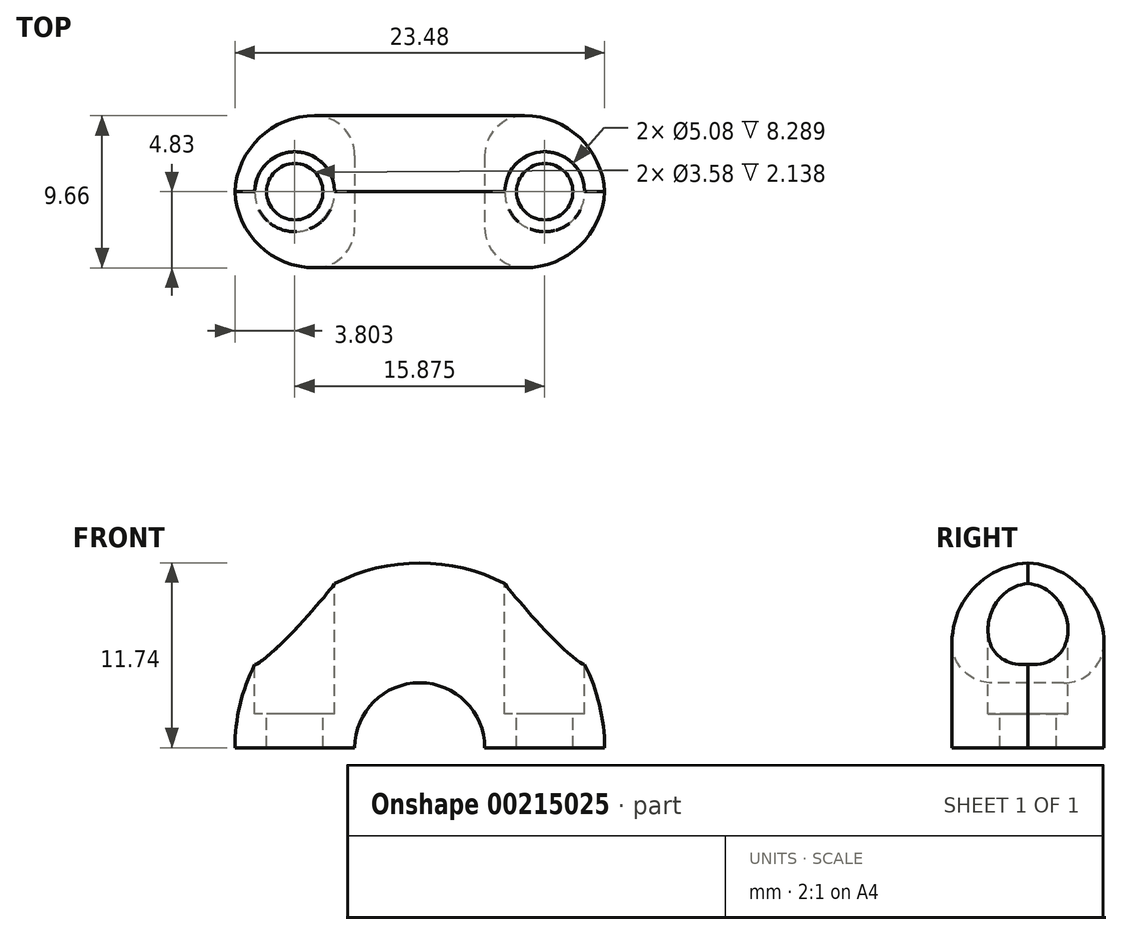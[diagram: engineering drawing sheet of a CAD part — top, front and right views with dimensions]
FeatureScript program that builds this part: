
annotation { "Feature Type Name" : "Feature", "Feature Type Description" : "" }
export const myFeature = defineFeature(function(context is Context, id is Id, definition is map)
    precondition{}
    {
        {
            var Q0;
            Q0=qCreatedBy(makeId("Top.planeOp"),FACE);
            var sketch = newSketch(context, id + "F0", { "sketchPlane" : qUnion([Q0])});
            skCircle(sketch, "E0", {"center": v(0, 0) * mm, "radius": 7.94 * mm, "construction": true});
            skCircle(sketch, "E1", {"center": v(-7.94, 0) * mm, "radius": 1.8 * mm});
            skLineSegment(sketch, "E2.bottom", {"start": v(14.29, 4.83) * mm, "end": v(-14.29, 4.83) * mm});
            skLineSegment(sketch, "E2.top", {"start": v(14.29, -4.83) * mm, "end": v(-14.29, -4.83) * mm});
            skLineSegment(sketch, "E2.left", {"start": v(14.29, 4.83) * mm, "end": v(14.29, -4.83) * mm});
            skLineSegment(sketch, "E2.right", {"start": v(-14.29, 4.83) * mm, "end": v(-14.29, -4.83) * mm});
            skCircle(sketch, "E3", {"center": v(-7.94, 0) * mm, "radius": 3.81 * mm});
            skLineSegment(sketch, "E4", {"start": v(0, 0) * mm, "end": v(0, 13.84) * mm, "construction": true});
            skCircle(sketch, "E5.MirrorC", {"center": v(7.94, 0) * mm, "radius": 1.8 * mm});
            skCircle(sketch, "E6.MirrorC", {"center": v(7.94, 0) * mm, "radius": 3.81 * mm});
            skLineSegment(sketch, "E7.bottom", {"start": v(-11.75, 4.83) * mm, "end": v(-4.13, 4.83) * mm});
            skLineSegment(sketch, "E7.top", {"start": v(-11.75, -4.83) * mm, "end": v(-4.13, -4.83) * mm});
            skLineSegment(sketch, "E7.left", {"start": v(-11.75, 4.83) * mm, "end": v(-11.75, -4.83) * mm});
            skLineSegment(sketch, "E7.right", {"start": v(-4.13, 4.83) * mm, "end": v(-4.13, -4.83) * mm});
            skSolve(sketch);
        }
        {
            var Q0;
            Q0=makeQuery(id+"F0.imprint","IMPRINT",FACE,{"disambiguationData":[TD([[makeQuery(id+"F0.imprint","IMPRINT",EDGE,{"derivedFrom":sQuery(id+"F0.wireOp",EDGE,"E1")}),-1.0]])]});
            var Q1;
            Q1=makeQuery(id+"F0.imprint","IMPRINT",FACE,{"disambiguationData":[TD([[makeQuery(id+"F0.imprint","IMPRINT",EDGE,{"derivedFrom":sQuery(id+"F0.wireOp",EDGE,"E1")}),1.0]])]});
            var Q2;
            Q2=makeQuery(id+"F0.imprint","IMPRINT",FACE,{"disambiguationData":[TD([[makeQuery(id+"F0.imprint","IMPRINT",EDGE,{"derivedFrom":sQuery(id+"F0.wireOp",EDGE,"E3")}),-1.0]])]});
            var Q3;
            Q3=sQuery(id+"F0.wireOp",EDGE,"E4");
            revolve(context, id + "F1", {"entities" : qUnion([Q0, Q1, Q2]), "axis" : qUnion([Q3]), "revolveType" : RevolveType.ONE_DIRECTION, "angle" : 180 * degree});
        }
        {
            var Q0;
            Q0=qCreatedBy(makeId("Top.planeOp"),FACE);
            cPlane(context, id + "F2", {"entities" : qUnion([Q0]), "cplaneType" : CPlaneType.OFFSET, "offset" : 12.7 * mm, "width" : 152.4 * mm, "height" : 152.4 * mm});
        }
        {
            var Q0;
            Q0=qCreatedBy(id+"F2.planeOp",FACE);
            var sketch = newSketch(context, id + "F3", { "sketchPlane" : qUnion([Q0])});
            skCircle(sketch, "E8", {"center": v(0, 0) * mm, "radius": 4.45 * mm});
            skCircle(sketch, "E9", {"center": v(0, 0) * mm, "radius": 7.94 * mm, "construction": true});
            skPoint(sketch, "E10", {"position": v(-7.94, 0) * mm});
            skPoint(sketch, "E11", {"position": v(7.94, 0) * mm});
            skSolve(sketch);
        }
        {
            var Q0;
            Q0=sQuery(id+"F3.wireOp",VERTEX,"E10");
            var Q1;
            Q1=sQuery(id+"F3.wireOp",VERTEX,"E11");
            var Q2;
            Q2=makeQuery(id+"F1.opRevolve","SWEPT_BODY",BODY,{"disambiguationData":[OSD([sQuery(id+"F0.wireOp",EDGE,"E7.bottom"),sQuery(id+"F0.wireOp",EDGE,"E7.top"),sQuery(id+"F0.wireOp",EDGE,"E7.left"),sQuery(id+"F0.wireOp",EDGE,"E7.right")])]});
            hole(context, id + "F4", {"style" : HoleStyle.C_BORE, "endStyle" : HoleEndStyle.BLIND, "holeDiameter" : 3.58 * mm, "cBoreDiameter" : 5.08 * mm, "cBoreDepth" : 3.17 * mm, "holeDepth" : 9.65 * mm, "locations" : qUnion([Q0, Q1]), "scope" : qUnion([Q2])});
        }
        {
            var Q0;
            Q0=makeQuery(id+"F1.opRevolve","SWEPT_EDGE",EDGE,{"disambiguationData":[OSD([sQuery(id+"F0.wireOp",EDGE,"E2.top"),sQuery(id+"F0.wireOp",EDGE,"E7.top"),sQuery(id+"F0.wireOp",EDGE,"E7.left")])]});
            var Q1;
            Q1=makeQuery(id+"F1.opRevolve","SWEPT_EDGE",EDGE,{"disambiguationData":[OSD([sQuery(id+"F0.wireOp",EDGE,"E2.bottom"),sQuery(id+"F0.wireOp",EDGE,"E7.bottom"),sQuery(id+"F0.wireOp",EDGE,"E7.left")])]});
            fillet(context, id + "F5", {"entities" : qUnion([Q0, Q1]), "radius" : 5.08 * mm, "tangentPropagation" : true, "allowEdgeOverflow" : false});
        }
        {
            var Q0;
            Q0=makeQuery(id+"F1.opRevolve","SWEPT_EDGE",EDGE,{"disambiguationData":[OSD([sQuery(id+"F0.wireOp",EDGE,"E2.top"),sQuery(id+"F0.wireOp",EDGE,"E7.top"),sQuery(id+"F0.wireOp",EDGE,"E7.right")])]});
            var Q1;
            Q1=makeQuery(id+"F1.opRevolve","SWEPT_EDGE",EDGE,{"disambiguationData":[OSD([sQuery(id+"F0.wireOp",EDGE,"E2.bottom"),sQuery(id+"F0.wireOp",EDGE,"E7.bottom"),sQuery(id+"F0.wireOp",EDGE,"E7.right")])]});
            fillet(context, id + "F6", {"entities" : qUnion([Q0, Q1]), "radius" : 2.54 * mm, "tangentPropagation" : true, "allowEdgeOverflow" : false});
        }
    });
